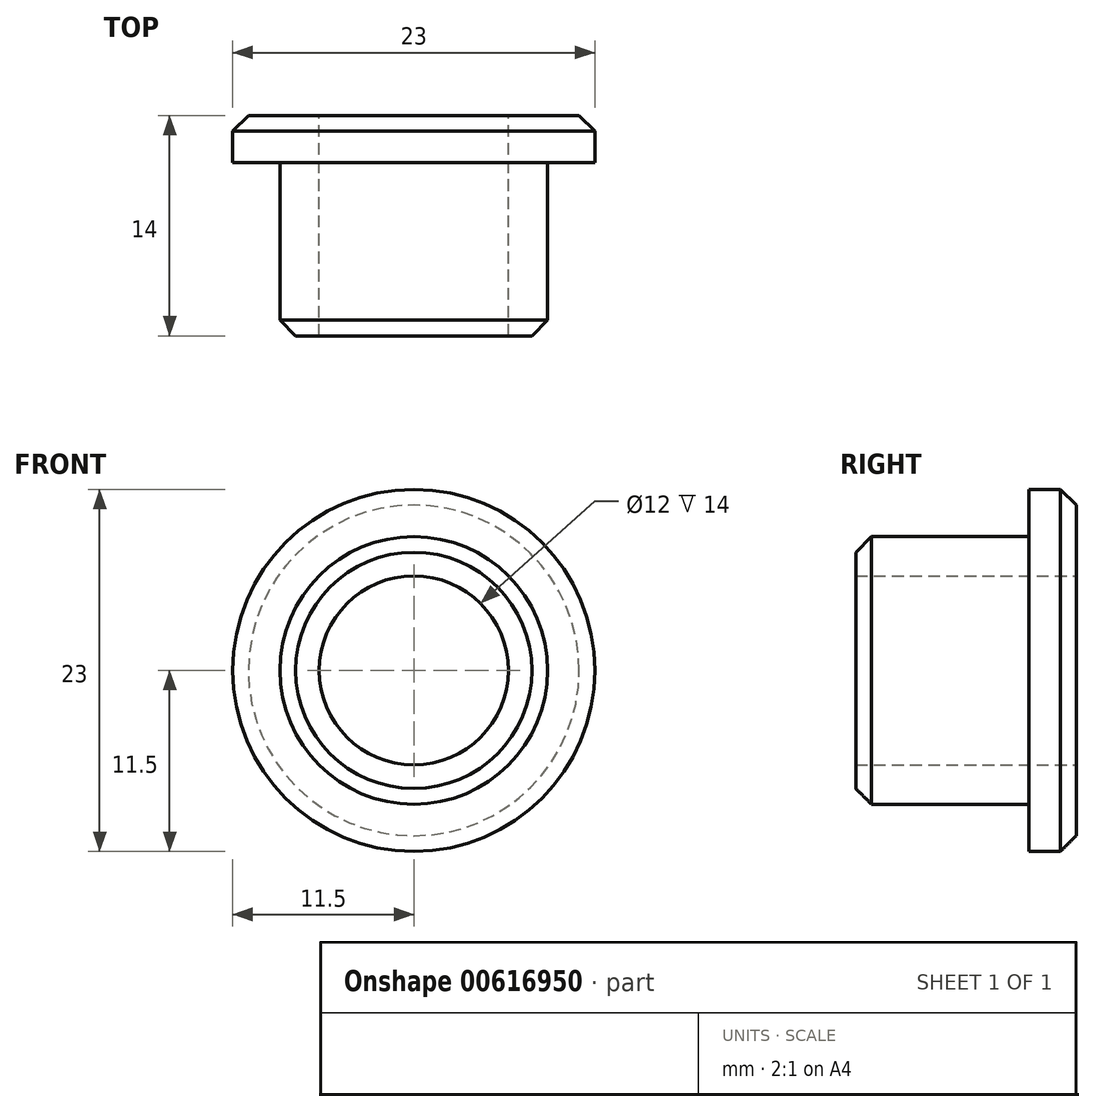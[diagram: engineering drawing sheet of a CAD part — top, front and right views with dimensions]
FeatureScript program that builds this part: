
annotation { "Feature Type Name" : "Feature", "Feature Type Description" : "" }
export const myFeature = defineFeature(function(context is Context, id is Id, definition is map)
    precondition{}
    {
        {
            var Q0;
            Q0=qCreatedBy(makeId("Front.planeOp"),FACE);
            var sketch = newSketch(context, id + "F0", { "sketchPlane" : qUnion([Q0])});
            skCircle(sketch, "E0", {"center": v(0, 0) * mm, "radius": 6 * mm});
            skCircle(sketch, "E1", {"center": v(0, 0) * mm, "radius": 8.5 * mm});
            skCircle(sketch, "E2", {"center": v(0, 0) * mm, "radius": 11.5 * mm});
            skSolve(sketch);
        }
        {
            var Q0;
            Q0 = qSketchRegion(id + "F0", true);
            extrude(context, id + "F1", {"entities" : qUnion([Q0]), "depth" : 3 * mm, "offsetDistance" : 25 * mm});
        }
        {
            var Q0;
            Q0=makeQuery(id+"F0.imprint","IMPRINT",FACE,{"disambiguationData":[TD([[makeQuery(id+"F0.imprint","IMPRINT",EDGE,{"derivedFrom":sQuery(id+"F0.wireOp",EDGE,"E0")}),-1.0]])]});
            extrude(context, id + "F2", {"entities" : qUnion([Q0]), "operationType" : NewBodyOperationType.ADD, "depth" : 14 * mm, "offsetDistance" : 25 * mm});
        }
        {
            var Q0;
            Q0=makeQuery(id+"F2.opExtrude","CAP_EDGE",EDGE,{"disambiguationData":[OSD([sQuery(id+"F0.wireOp",EDGE,"E1")])],"isStart":false});
            var Q1;
            Q1=makeQuery(id+"F1.opExtrude","CAP_EDGE",EDGE,{"disambiguationData":[OSD([sQuery(id+"F0.wireOp",EDGE,"E2")])],"isStart":true});
            chamfer(context, id + "F3", {"entities" : qUnion([Q0, Q1]), "width" : 1 * mm, "tangentPropagation" : true});
        }
    });
